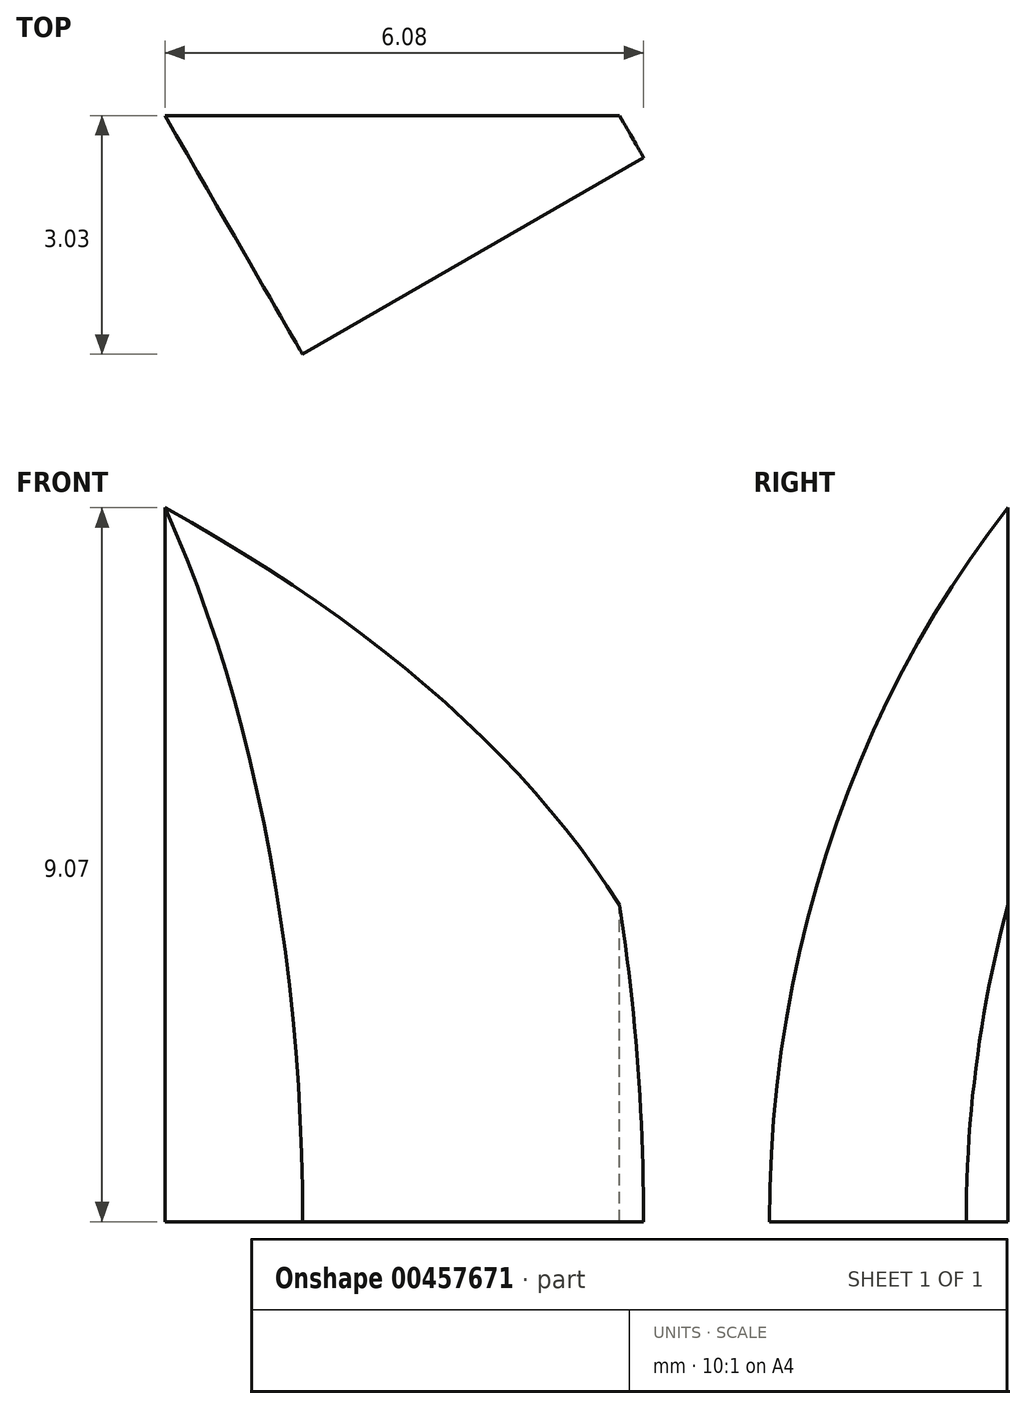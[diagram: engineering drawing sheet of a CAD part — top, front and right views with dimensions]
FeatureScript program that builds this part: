
annotation { "Feature Type Name" : "Feature", "Feature Type Description" : "" }
export const myFeature = defineFeature(function(context is Context, id is Id, definition is map)
    precondition{}
    {
        {
            var Q0;
            Q0=qCreatedBy(makeId("Top.planeOp"),FACE);
            var sketch = newSketch(context, id + "F0", { "sketchPlane" : qUnion([Q0])});
            skCircle(sketch, "E0.cCircle", {"center": v(0, 0) * mm, "radius": 20 * mm, "construction": true});
            skLineSegment(sketch, "E0.0", {"start": v(20, 0) * mm, "end": v(10, -17.32) * mm});
            skLineSegment(sketch, "E0.1", {"start": v(10, -17.32) * mm, "end": v(-10, -17.32) * mm});
            skLineSegment(sketch, "E0.2", {"start": v(-10, -17.32) * mm, "end": v(-20, 0) * mm});
            skLineSegment(sketch, "E0.3", {"start": v(-20, 0) * mm, "end": v(-10, 17.32) * mm});
            skLineSegment(sketch, "E0.4", {"start": v(-10, 17.32) * mm, "end": v(10, 17.32) * mm});
            skLineSegment(sketch, "E0.5", {"start": v(10, 17.32) * mm, "end": v(20, 0) * mm});
            skCircle(sketch, "E1.cCircle", {"center": v(0, 0) * mm, "radius": 28 * mm, "construction": true});
            skLineSegment(sketch, "E1.0", {"start": v(28, 0) * mm, "end": v(14, -24.25) * mm});
            skLineSegment(sketch, "E1.1", {"start": v(14, -24.25) * mm, "end": v(-14, -24.25) * mm});
            skLineSegment(sketch, "E1.2", {"start": v(-14, -24.25) * mm, "end": v(-28, 0) * mm});
            skLineSegment(sketch, "E1.3", {"start": v(-28, 0) * mm, "end": v(-14, 24.25) * mm});
            skLineSegment(sketch, "E1.4", {"start": v(-14, 24.25) * mm, "end": v(14, 24.25) * mm});
            skLineSegment(sketch, "E1.5", {"start": v(14, 24.25) * mm, "end": v(28, 0) * mm});
            skLineSegment(sketch, "E2", {"start": v(10, 17.32) * mm, "end": v(6, 24.25) * mm});
            skLineSegment(sketch, "E3", {"start": v(20, 0) * mm, "end": v(24, -6.93) * mm});
            skLineSegment(sketch, "E4", {"start": v(20, 0) * mm, "end": v(24, 6.93) * mm});
            skLineSegment(sketch, "E5", {"start": v(10, -17.32) * mm, "end": v(6, -24.25) * mm});
            skLineSegment(sketch, "E6", {"start": v(10, -17.32) * mm, "end": v(18, -17.32) * mm});
            skLineSegment(sketch, "E7", {"start": v(-10, -17.32) * mm, "end": v(-18, -17.32) * mm});
            skLineSegment(sketch, "E8", {"start": v(-10, -17.32) * mm, "end": v(-6, -24.25) * mm});
            skLineSegment(sketch, "E9", {"start": v(-20, 0) * mm, "end": v(-24, 6.93) * mm});
            skLineSegment(sketch, "E10", {"start": v(-20, 0) * mm, "end": v(-24, -6.93) * mm});
            skLineSegment(sketch, "E11", {"start": v(-10, 17.32) * mm, "end": v(-6, 24.25) * mm});
            skLineSegment(sketch, "E12", {"start": v(-10, 17.32) * mm, "end": v(-18, 17.32) * mm});
            skLineSegment(sketch, "E13", {"start": v(10, 17.32) * mm, "end": v(18, 17.32) * mm});
            skLineSegment(sketch, "E14", {"start": v(-20.89, -12.32) * mm, "end": v(20.89, -12.32) * mm});
            skSolve(sketch);
        }
        {
            var Q0;
            {var subQ4=sQuery(id+"F0.wireOp",EDGE,"E7");Q0=makeQuery(id+"F0.imprint","IMPRINT",FACE,{"disambiguationData":[TD([[makeQuery(id+"F0.imprint","IMPRINT",EDGE,{"derivedFrom":subQ4}),1.0]])]});}
            extrude(context, id + "F1", {"entities" : qUnion([Q0]), "endBound" : BoundingType.SYMMETRIC, "depth" : 36 * mm});
        }
        {
            var Q0;
            Q0=sQuery(id+"F0.wireOp",EDGE,"E0.1");
            extrude(context, id + "F2", {"bodyType" : ToolBodyType.SURFACE, "surfaceEntities" : qUnion([Q0]), "endBound" : BoundingType.SYMMETRIC, "depth" : 36 * mm});
        }
        {
            var Q0;
            Q0=makeQuery(id+"F2.opExtrude","SWEPT_FACE",FACE,{"disambiguationData":[OSD([sQuery(id+"F0.wireOp",EDGE,"E0.1")])]});
            var sketch = newSketch(context, id + "F3", { "sketchPlane" : qUnion([Q0])});
            skCircle(sketch, "E15", {"center": v(0, 0) * mm, "radius": 13.5 * mm});
            skLineSegment(sketch, "E16", {"start": v(-10, 13.5) * mm, "end": v(10, 13.5) * mm, "construction": true});
            skSolve(sketch);
        }
        {
            var Q0;
            Q0=qSketchRegion(id+"F3",true);
            extrude(context, id + "F4", {"entities" : qUnion([Q0]), "depth" : 5 * mm});
        }
        {
            var Q0;
            Q0=sQuery(id+"F0.wireOp",EDGE,"E0.2");
            extrude(context, id + "F5", {"bodyType" : ToolBodyType.SURFACE, "surfaceEntities" : qUnion([Q0]), "endBound" : BoundingType.SYMMETRIC, "depth" : 36 * mm});
        }
        {
            var Q0;
            Q0=makeQuery(id+"F5.opExtrude","SWEPT_FACE",FACE,{"disambiguationData":[OSD([sQuery(id+"F0.wireOp",EDGE,"E0.2")])]});
            var sketch = newSketch(context, id + "F6", { "sketchPlane" : qUnion([Q0])});
            skCircle(sketch, "E17", {"center": v(0, 0) * mm, "radius": 13.5 * mm});
            skLineSegment(sketch, "E18", {"start": v(-10, 13.5) * mm, "end": v(10, 13.5) * mm, "construction": true});
            skSolve(sketch);
        }
        {
            var Q0;
            Q0=qSketchRegion(id+"F6",true);
            extrude(context, id + "F7", {"entities" : qUnion([Q0]), "operationType" : NewBodyOperationType.INTERSECT, "depth" : 5 * mm});
        }
        {
            var Q0;
            Q0=qSketchRegion(id+"F3",true);
            extrude(context, id + "F8", {"entities" : qUnion([Q0]), "depth" : 5 * mm});
        }
        {
            var Q0;
            Q0=makeQuery(id+"F5.opExtrude","SWEPT_FACE",FACE,{"disambiguationData":[OSD([sQuery(id+"F0.wireOp",EDGE,"E0.2")])]});
            var sketch = newSketch(context, id + "F9", { "sketchPlane" : qUnion([Q0])});
            skLineSegment(sketch, "E19.bottom", {"start": v(30, 18) * mm, "end": v(-30, 18) * mm});
            skLineSegment(sketch, "E19.top", {"start": v(30, -18) * mm, "end": v(-30, -18) * mm});
            skLineSegment(sketch, "E19.left", {"start": v(30, 18) * mm, "end": v(30, -18) * mm});
            skLineSegment(sketch, "E19.right", {"start": v(-30, 18) * mm, "end": v(-30, -18) * mm});
            skSolve(sketch);
        }
        {
            var Q0;
            Q0=qSketchRegion(id+"F9",true);
            extrude(context, id + "F10", {"entities" : qUnion([Q0]), "operationType" : NewBodyOperationType.REMOVE, "depth" : 25 * mm});
        }
        {
            var Q0;
            Q0=qSketchRegion(id+"F6",true);
            extrude(context, id + "F11", {"entities" : qUnion([Q0]), "depth" : 5 * mm});
        }
        {
            var Q0;
            Q0=makeQuery(id+"F2.opExtrude","SWEPT_FACE",FACE,{"disambiguationData":[OSD([sQuery(id+"F0.wireOp",EDGE,"E0.1")])]});
            var sketch = newSketch(context, id + "F12", { "sketchPlane" : qUnion([Q0])});
            skLineSegment(sketch, "E20.bottom", {"start": v(-30, 18) * mm, "end": v(30, 18) * mm});
            skLineSegment(sketch, "E20.top", {"start": v(-30, -18) * mm, "end": v(30, -18) * mm});
            skLineSegment(sketch, "E20.left", {"start": v(-30, 18) * mm, "end": v(-30, -18) * mm});
            skLineSegment(sketch, "E20.right", {"start": v(30, 18) * mm, "end": v(30, -18) * mm});
            skSolve(sketch);
        }
        {
            var Q0;
            Q0=qSketchRegion(id+"F12",true);
            extrude(context, id + "F13", {"entities" : qUnion([Q0]), "operationType" : NewBodyOperationType.REMOVE, "depth" : 25 * mm});
        }
        {
            var Q0;
            Q0=qCreatedBy(makeId("Top.planeOp"),FACE);
            var sketch = newSketch(context, id + "F14", { "sketchPlane" : qUnion([Q0])});
            skLineSegment(sketch, "E21.bottom", {"start": v(100, -60) * mm, "end": v(-100, -60) * mm});
            skLineSegment(sketch, "E21.top", {"start": v(100, 60) * mm, "end": v(-100, 60) * mm});
            skLineSegment(sketch, "E21.left", {"start": v(100, -60) * mm, "end": v(100, 60) * mm});
            skLineSegment(sketch, "E21.right", {"start": v(-100, -60) * mm, "end": v(-100, 60) * mm});
            skPoint(sketch, "E21.middle", {"position": v(0, 0) * mm});
            skSolve(sketch);
        }
        {
            var Q0;
            Q0=qSketchRegion(id+"F14",true);
            extrude(context, id + "F15", {"entities" : qUnion([Q0]), "operationType" : NewBodyOperationType.REMOVE, "oppositeDirection" : true, "depth" : 25 * mm});
        }
    });
